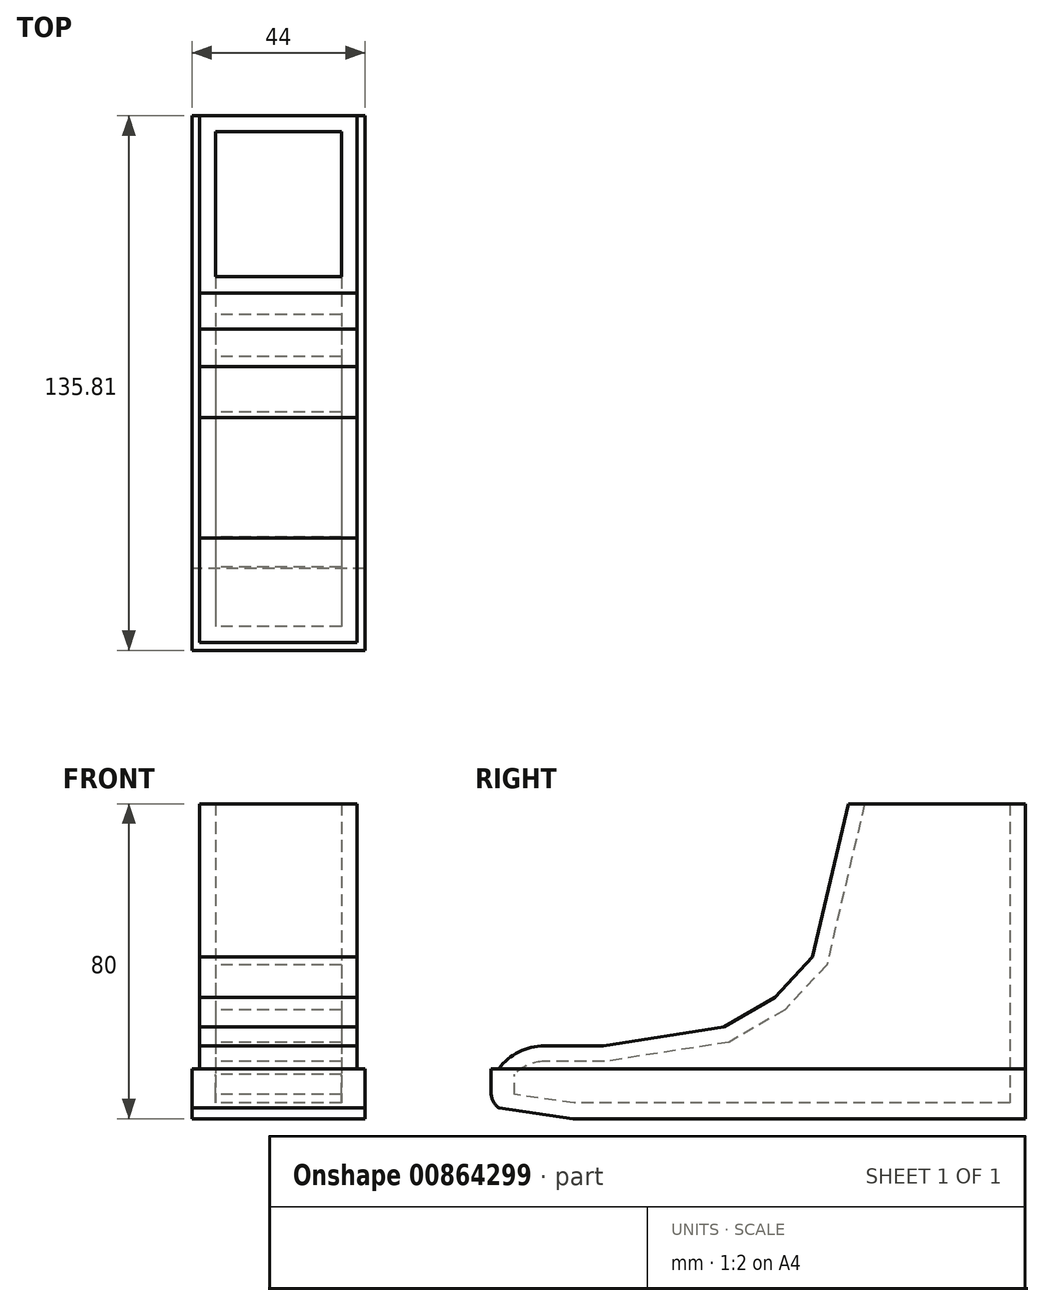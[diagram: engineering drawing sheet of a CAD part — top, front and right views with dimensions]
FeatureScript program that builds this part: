
annotation { "Feature Type Name" : "Feature", "Feature Type Description" : "" }
export const myFeature = defineFeature(function(context is Context, id is Id, definition is map)
    precondition{}
    {
        {
            var Q0;
            Q0=qCreatedBy(makeId("Right.planeOp"),FACE);
            var sketch = newSketch(context, id + "F0", { "sketchPlane" : qUnion([Q0])});
            skLineSegment(sketch, "E0", {"start": v(63.7, 38.94) * mm, "end": v(63.7, -41.06) * mm});
            skLineSegment(sketch, "E1", {"start": v(63.7, -41.06) * mm, "end": v(-51.3, -41.06) * mm});
            skLineSegment(sketch, "E2", {"start": v(63.7, 38.94) * mm, "end": v(18.7, 38.94) * mm});
            skLineSegment(sketch, "E3", {"start": v(18.7, 38.94) * mm, "end": v(9.53, 0) * mm});
            skLineSegment(sketch, "E4", {"start": v(9.53, 0) * mm, "end": v(0, -10.26) * mm});
            skLineSegment(sketch, "E5", {"start": v(0, -10.26) * mm, "end": v(-12.98, -17.78) * mm});
            skLineSegment(sketch, "E6", {"start": v(-12.98, -17.78) * mm, "end": v(-43.6, -22.56) * mm});
            skLineSegment(sketch, "E7", {"start": v(-51.3, -41.06) * mm, "end": v(-70.12, -38.37) * mm});
            skLineSegment(sketch, "E8", {"start": v(-70.12, -38.37) * mm, "end": v(-70.12, -28.37) * mm});
            skLineSegment(sketch, "E9", {"start": v(-51.31, -31.1) * mm, "end": v(-70.12, -28.37) * mm});
            skLineSegment(sketch, "E10", {"start": v(-51.31, -31.1) * mm, "end": v(63.7, -31.1) * mm});
            skLineSegment(sketch, "E11", {"start": v(-43.6, -22.56) * mm, "end": v(-58.6, -22.56) * mm});
            skArc(sketch, "E12", {"start": v(-58.6, -22.56) * mm, "mid": v(-65.05, -24.1) * mm, "end": v(-70.12, -28.37) * mm});
            skCircle(sketch, "E13", {"center": v(47.84, 10.78) * mm, "radius": 11 * mm});
            skCircle(sketch, "E14", {"center": v(47.84, 10.78) * mm, "radius": 8.5 * mm});
            skLineSegment(sketch, "E15", {"start": v(47.84, 10.78) * mm, "end": v(47.84, 14.78) * mm});
            skLineSegment(sketch, "E16", {"start": v(47.84, 14.78) * mm, "end": v(49.12, 10.78) * mm});
            skLineSegment(sketch, "E17", {"start": v(47.84, 14.78) * mm, "end": v(46.56, 10.78) * mm});
            skLineSegment(sketch, "E18", {"start": v(46.56, 10.78) * mm, "end": v(42.56, 10.78) * mm});
            skLineSegment(sketch, "E19", {"start": v(42.56, 10.78) * mm, "end": v(46.56, 8.72) * mm});
            skLineSegment(sketch, "E20", {"start": v(49.12, 10.78) * mm, "end": v(53.12, 10.78) * mm});
            skLineSegment(sketch, "E21", {"start": v(49.12, 8.76) * mm, "end": v(53.12, 10.78) * mm});
            skSolve(sketch);
        }
        {
            var Q0;
            {var subQ1=sQuery(id+"F0.wireOp",EDGE,"E2");Q0=makeQuery(id+"F0.imprint","IMPRINT",FACE,{"disambiguationData":[TD([[makeQuery(id+"F0.imprint","IMPRINT",EDGE,{"derivedFrom":subQ1}),1.0]])]});}
            var Q1;
            {var subQ0=sQuery(id+"F0.wireOp",EDGE,"E1");Q1=makeQuery(id+"F0.imprint","IMPRINT",FACE,{"disambiguationData":[TD([[makeQuery(id+"F0.imprint","IMPRINT",EDGE,{"derivedFrom":subQ0}),-1.0]])]});}
            var Q2;
            {var subQ1=sQuery(id+"F0.wireOp",EDGE,"E9");Q2=makeQuery(id+"F0.imprint","IMPRINT",FACE,{"disambiguationData":[TD([[makeQuery(id+"F0.imprint","IMPRINT",EDGE,{"derivedFrom":subQ1}),-1.0]])]});}
            var Q3;
            Q3=makeQuery(id+"F0.imprint","IMPRINT",FACE,{"disambiguationData":[TD([[makeQuery(id+"F0.imprint","IMPRINT",EDGE,{"derivedFrom":sQuery(id+"F0.wireOp",EDGE,"E14")}),1.0]])]});
            var Q4;
            Q4=makeQuery(id+"F0.imprint","IMPRINT",FACE,{"disambiguationData":[TD([[makeQuery(id+"F0.imprint","IMPRINT",EDGE,{"derivedFrom":sQuery(id+"F0.wireOp",EDGE,"E13")}),1.0]])]});
            extrude(context, id + "F1", {"entities" : qUnion([Q0, Q1, Q2, Q3, Q4]), "depth" : 40 * mm, "offsetDistance" : 25 * mm});
        }
        {
            var Q0;
            Q0=makeQuery(id+"F1.opExtrude","SWEPT_FACE",FACE,{"disambiguationData":[OSD([sQuery(id+"F0.wireOp",EDGE,"E2")])]});
            shell(context, id + "F2", {"entities" : qUnion([Q0]), "thickness" : 4 * mm});
        }
        {
            var Q0;
            Q0=makeQuery(id+"F1.opExtrude","SWEPT_FACE",FACE,{"disambiguationData":[OSD([sQuery(id+"F0.wireOp",EDGE,"E8")])]});
            extrude(context, id + "F3", {"entities" : qUnion([Q0]), "operationType" : NewBodyOperationType.ADD, "depth" : 2 * mm, "offsetDistance" : 25 * mm});
        }
        {
            var Q0;
            {var subQ0=sQuery(id+"F0.wireOp",EDGE,"E8");Q0=makeQuery(id+"F3.boolean.opBoolean","MERGE",FACE,{"derivedFrom":[makeQuery(id+"F1.opExtrude","CAP_FACE",FACE,{"disambiguationData":[OSD([sQuery(id+"F0.wireOp",EDGE,"E0"),sQuery(id+"F0.wireOp",EDGE,"E1"),sQuery(id+"F0.wireOp",EDGE,"E2"),sQuery(id+"F0.wireOp",EDGE,"E3"),sQuery(id+"F0.wireOp",EDGE,"E4"),sQuery(id+"F0.wireOp",EDGE,"E5"),sQuery(id+"F0.wireOp",EDGE,"E6"),sQuery(id+"F0.wireOp",EDGE,"E7"),subQ0,sQuery(id+"F0.wireOp",EDGE,"E11"),sQuery(id+"F0.wireOp",EDGE,"E12")])],"isStart":false}),makeQuery(id+"F3.opExtrude","SWEPT_FACE",FACE,{"disambiguationData":[OSD([subQ0]),TDD([makeQuery(id+"F1.opExtrude","CAP_EDGE",EDGE,{"disambiguationData":[OSD([subQ0])],"isStart":false})])]})]});}
            var sketch = newSketch(context, id + "F4", { "sketchPlane" : qUnion([Q0])});
            skLineSegment(sketch, "E22", {"start": v(-70.12, -28.37) * mm, "end": v(63.7, -28.37) * mm});
            skSolve(sketch);
        }
        {
            var Q0;
            Q0 = qSketchRegion(id + "F4", true);
            var Q1;
            {var subQ3=sQuery(id+"F4.wireOp",EDGE,"E22");Q1=makeQuery(id+"F4.imprint","IMPRINT",FACE,{"disambiguationData":[TD([[makeQuery(id+"F4.imprint","IMPRINT",EDGE,{"derivedFrom":subQ3}),-1.0]])]});}
            extrude(context, id + "F5", {"entities" : qUnion([Q0, Q1]), "operationType" : NewBodyOperationType.ADD, "depth" : 2 * mm, "offsetDistance" : 25 * mm});
        }
        {
            var Q0;
            {var subQ0=sQuery(id+"F0.wireOp",EDGE,"E8");Q0=makeQuery(id+"F3.boolean.opBoolean","MERGE",FACE,{"derivedFrom":[makeQuery(id+"F1.opExtrude","CAP_FACE",FACE,{"disambiguationData":[OSD([sQuery(id+"F0.wireOp",EDGE,"E0"),sQuery(id+"F0.wireOp",EDGE,"E1"),sQuery(id+"F0.wireOp",EDGE,"E2"),sQuery(id+"F0.wireOp",EDGE,"E3"),sQuery(id+"F0.wireOp",EDGE,"E4"),sQuery(id+"F0.wireOp",EDGE,"E5"),sQuery(id+"F0.wireOp",EDGE,"E6"),sQuery(id+"F0.wireOp",EDGE,"E7"),subQ0,sQuery(id+"F0.wireOp",EDGE,"E11"),sQuery(id+"F0.wireOp",EDGE,"E12")])],"isStart":true}),makeQuery(id+"F3.opExtrude","SWEPT_FACE",FACE,{"disambiguationData":[OSD([subQ0]),TDD([makeQuery(id+"F1.opExtrude","CAP_EDGE",EDGE,{"disambiguationData":[OSD([subQ0])],"isStart":true})])]})]});}
            var sketch = newSketch(context, id + "F6", { "sketchPlane" : qUnion([Q0])});
            skLineSegment(sketch, "E23", {"start": v(70.12, -28.37) * mm, "end": v(-63.7, -28.37) * mm});
            skSolve(sketch);
        }
        {
            var Q0;
            Q0 = qSketchRegion(id + "F6", true);
            var Q1;
            {var subQ3=sQuery(id+"F6.wireOp",EDGE,"E23");Q1=makeQuery(id+"F6.imprint","IMPRINT",FACE,{"disambiguationData":[TD([[makeQuery(id+"F6.imprint","IMPRINT",EDGE,{"derivedFrom":subQ3}),1.0]])]});}
            extrude(context, id + "F7", {"entities" : qUnion([Q0, Q1]), "operationType" : NewBodyOperationType.ADD, "depth" : 2 * mm, "offsetDistance" : 25 * mm});
        }
        {
            var Q0;
            {var subQ0=sQuery(id+"F0.wireOp",EDGE,"E8");var subQ1=sQuery(id+"F0.wireOp",EDGE,"E7");Q0=makeQuery(id+"F7.boolean.opBoolean","MERGE",EDGE,{"derivedFrom":[makeQuery(id+"F5.boolean.opBoolean","MERGE",EDGE,{"derivedFrom":[makeQuery(id+"F3.opExtrude","CAP_EDGE",EDGE,{"disambiguationData":[OSD([subQ1,subQ0])],"isStart":false}),makeQuery(id+"F5.opExtrude","SWEPT_EDGE",EDGE,{"disambiguationData":[OSD([subQ1,subQ0]),TDD([makeQuery(id+"F4.imprint","INTERSECT",VERTEX,{"derivedFrom":[makeQuery(id+"F3.opExtrude","SWEPT_EDGE",EDGE,{"disambiguationData":[OSD([subQ1,subQ0]),TDD([makeQuery(id+"F1.opExtrude","CAP_VERTEX",VERTEX,{"disambiguationData":[OSD([subQ1,subQ0])],"isStart":false})])]}),makeQuery(id+"F3.opExtrude","CAP_EDGE",EDGE,{"disambiguationData":[OSD([subQ0]),TDD([makeQuery(id+"F1.opExtrude","CAP_EDGE",EDGE,{"disambiguationData":[OSD([subQ0])],"isStart":false})])],"isStart":false})]})])]})]}),makeQuery(id+"F7.opExtrude","SWEPT_EDGE",EDGE,{"disambiguationData":[OSD([subQ1,subQ0]),TDD([makeQuery(id+"F6.imprint","INTERSECT",VERTEX,{"derivedFrom":[makeQuery(id+"F3.opExtrude","SWEPT_EDGE",EDGE,{"disambiguationData":[OSD([subQ1,subQ0]),TDD([makeQuery(id+"F1.opExtrude","CAP_VERTEX",VERTEX,{"disambiguationData":[OSD([subQ1,subQ0])],"isStart":true})])]}),makeQuery(id+"F3.opExtrude","CAP_EDGE",EDGE,{"disambiguationData":[OSD([subQ0]),TDD([makeQuery(id+"F1.opExtrude","CAP_EDGE",EDGE,{"disambiguationData":[OSD([subQ0])],"isStart":true})])],"isStart":false})]})])]})]});}
            fillet(context, id + "F8", {"entities" : qUnion([Q0]), "radius" : 5 * mm, "tangentPropagation" : true, "allowEdgeOverflow" : false});
        }
    });
